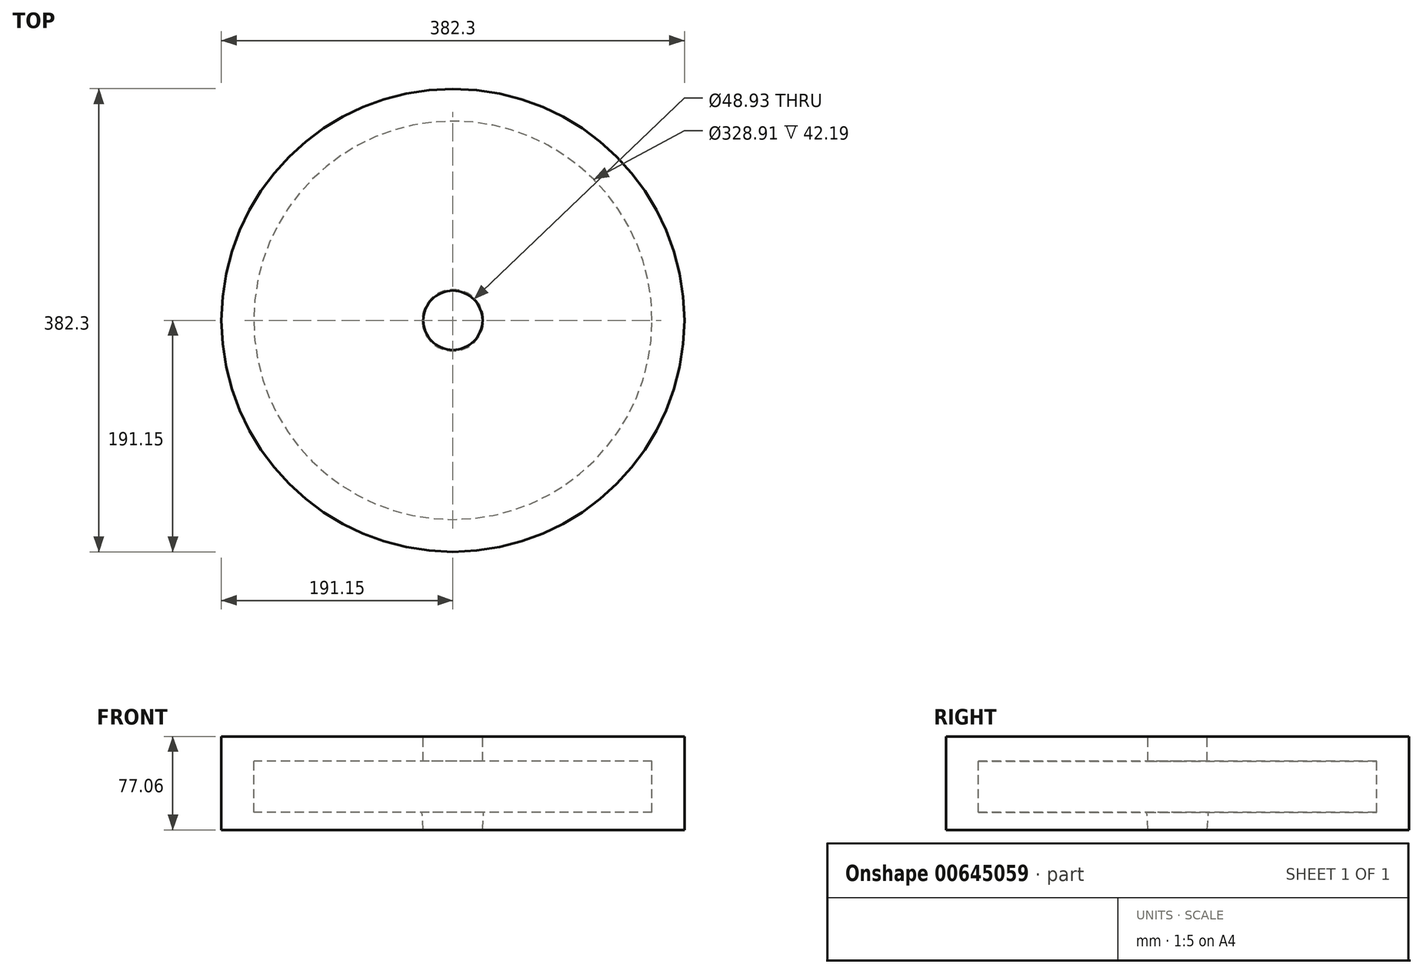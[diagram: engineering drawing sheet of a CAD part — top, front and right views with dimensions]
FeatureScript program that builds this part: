
annotation { "Feature Type Name" : "Feature", "Feature Type Description" : "" }
export const myFeature = defineFeature(function(context is Context, id is Id, definition is map)
    precondition{}
    {
        {
            var Q0;
            Q0=qCreatedBy(makeId("Front.planeOp"),FACE);
            var sketch = newSketch(context, id + "F0", { "sketchPlane" : qUnion([Q0])});
            skLineSegment(sketch, "E0.bottom", {"start": v(24.46, 42.24) * mm, "end": v(191.15, 42.24) * mm});
            skLineSegment(sketch, "E0.top", {"start": v(24.46, -34.82) * mm, "end": v(191.15, -34.82) * mm});
            skLineSegment(sketch, "E0.left", {"start": v(0, 42.24) * mm, "end": v(0, -34.82) * mm});
            skLineSegment(sketch, "E0.right", {"start": v(191.15, 42.24) * mm, "end": v(191.15, -34.82) * mm});
            skLineSegment(sketch, "E1.bottom", {"start": v(24.46, 22) * mm, "end": v(164.45, 22) * mm});
            skLineSegment(sketch, "E1.top", {"start": v(25.4, -20.18) * mm, "end": v(164.45, -20.18) * mm});
            skLineSegment(sketch, "E1.right", {"start": v(164.45, 22) * mm, "end": v(164.45, -20.18) * mm});
            skLineSegment(sketch, "E2", {"start": v(24.46, 73.6) * mm, "end": v(24.46, 22) * mm});
            skLineSegment(sketch, "E3.trimOffspring", {"start": v(24.46, -34.82) * mm, "end": v(24.46, -70.39) * mm});
            skLineSegment(sketch, "E4", {"start": v(25.4, -20.18) * mm, "end": v(24.46, -34.82) * mm});
            skSolve(sketch);
        }
        {
            var Q0;
            {var subQ1=sQuery(id+"F0.wireOp",EDGE,"E0.bottom");Q0=makeQuery(id+"F0.imprint","IMPRINT",FACE,{"disambiguationData":[TD([[makeQuery(id+"F0.imprint","IMPRINT",EDGE,{"derivedFrom":subQ1}),-1.0]])]});}
            var Q1;
            Q1=sQuery(id+"F0.wireOp",EDGE,"E0.left");
            revolve(context, id + "F1", {"entities" : qUnion([Q0]), "axis" : qUnion([Q1]), "revolveType" : RevolveType.FULL});
        }
    });
